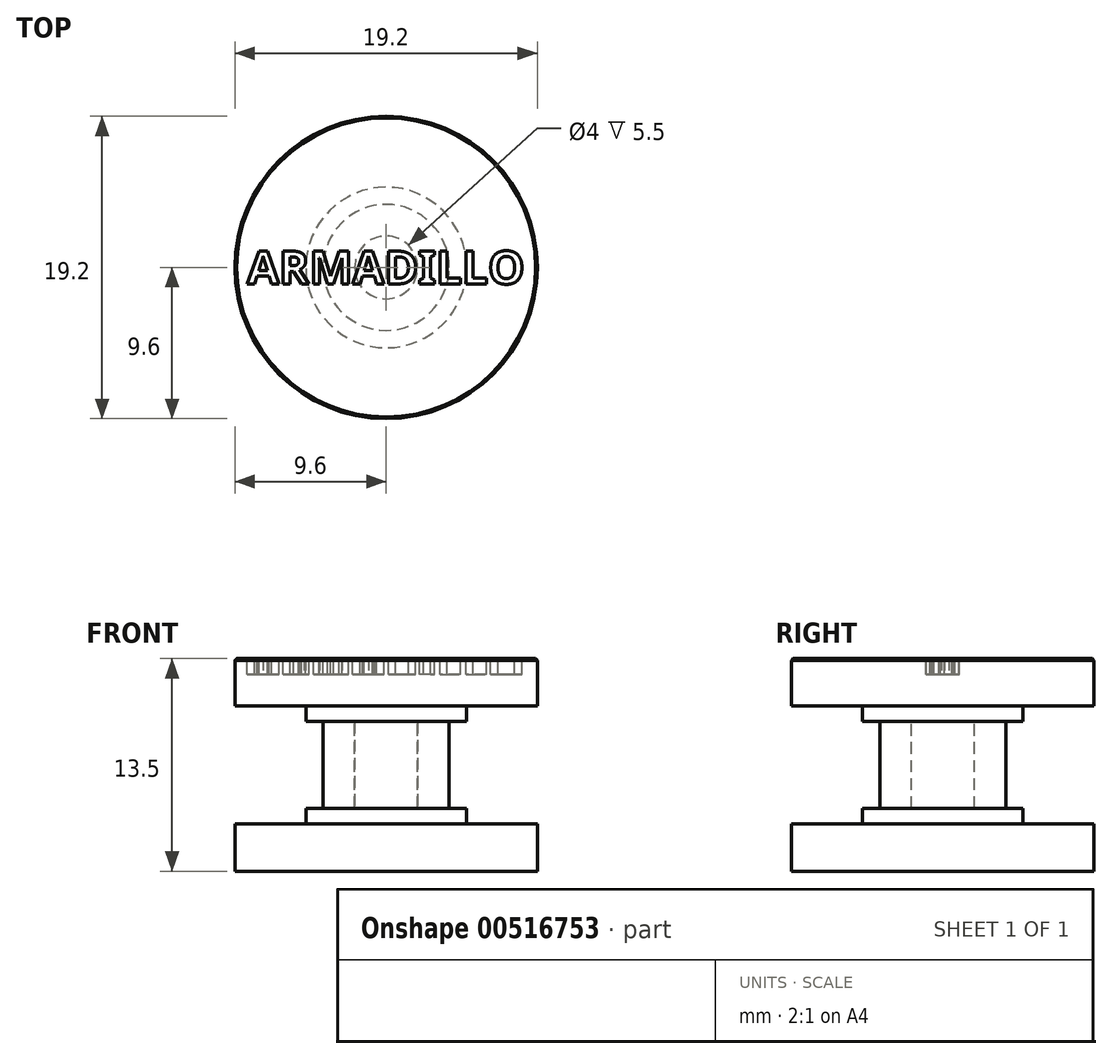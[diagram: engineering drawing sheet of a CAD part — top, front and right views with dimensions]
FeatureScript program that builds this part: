
annotation { "Feature Type Name" : "Feature", "Feature Type Description" : "" }
export const myFeature = defineFeature(function(context is Context, id is Id, definition is map)
    precondition{}
    {
        {
            var Q0;
            Q0=qCreatedBy(makeId("Front.planeOp"),FACE);
            var sketch = newSketch(context, id + "F0", { "sketchPlane" : qUnion([Q0])});
            skLineSegment(sketch, "E0", {"start": v(0, 5.5) * mm, "end": v(0, 9.5) * mm});
            skLineSegment(sketch, "E1", {"start": v(0, 9.5) * mm, "end": v(9.6, 9.5) * mm});
            skLineSegment(sketch, "E2", {"start": v(9.6, 9.5) * mm, "end": v(9.6, 6.5) * mm});
            skLineSegment(sketch, "E3", {"start": v(9.6, 6.5) * mm, "end": v(5.1, 6.5) * mm});
            skLineSegment(sketch, "E4", {"start": v(5.1, 6.5) * mm, "end": v(5.1, 5.5) * mm});
            skLineSegment(sketch, "E5", {"start": v(5.1, 5.5) * mm, "end": v(4, 5.5) * mm});
            skLineSegment(sketch, "E6", {"start": v(4, 5.5) * mm, "end": v(4, 0) * mm});
            skLineSegment(sketch, "E7", {"start": v(4, 0) * mm, "end": v(2, 0) * mm});
            skLineSegment(sketch, "E8.bottom", {"start": v(0, 5.5) * mm, "end": v(2, 5.5) * mm});
            skLineSegment(sketch, "E8.right", {"start": v(2, 5.5) * mm, "end": v(2, 0) * mm});
            skPoint(sketch, "E9.orphan", {"position": v(0, 0) * mm});
            skLineSegment(sketch, "E10.bottom", {"start": v(2, 0) * mm, "end": v(5.1, 0) * mm});
            skLineSegment(sketch, "E10.right", {"start": v(5.1, 0) * mm, "end": v(5.1, -1) * mm});
            skLineSegment(sketch, "E11.bottom", {"start": v(5.1, -1) * mm, "end": v(9.6, -1) * mm});
            skLineSegment(sketch, "E11.top", {"start": v(0, -4) * mm, "end": v(9.6, -4) * mm});
            skLineSegment(sketch, "E11.right", {"start": v(9.6, -1) * mm, "end": v(9.6, -4) * mm});
            skLineSegment(sketch, "E12", {"start": v(0, 5.5) * mm, "end": v(0, -4) * mm});
            skSolve(sketch);
        }
        {
            var Q0;
            Q0=makeQuery(id+"F0.imprint","IMPRINT",FACE,{"disambiguationData":[TD([[makeQuery(id+"F0.imprint","IMPRINT",EDGE,{"derivedFrom":sQuery(id+"F0.wireOp",EDGE,"E0")}),-1.0]])]});
            var Q1;
            Q1=sQuery(id+"F0.wireOp",EDGE,"E0");
            revolve(context, id + "F1", {"entities" : qUnion([Q0]), "axis" : qUnion([Q1]), "revolveType" : RevolveType.FULL});
        }
        {
            var Q0;
            Q0=makeQuery(id+"F1.opRevolve","SWEPT_EDGE",EDGE,{"disambiguationData":[OSD([sQuery(id+"F0.wireOp",EDGE,"E1"),sQuery(id+"F0.wireOp",EDGE,"E2")])]});
            chamfer(context, id + "F2", {"entities" : qUnion([Q0]), "width" : 0.1 * mm, "tangentPropagation" : true});
        }
        {
            var Q0;
            Q0=makeQuery(id+"F1.opRevolve","SWEPT_FACE",FACE,{"disambiguationData":[OSD([sQuery(id+"F0.wireOp",EDGE,"E1")])]});
            var sketch = newSketch(context, id + "F3", { "sketchPlane" : qUnion([Q0])});
            skText(sketch, "E13", { "text": "ARMADILLO", "fontName": "NotoSans-Bold.ttf"});
            skPoint(sketch, "E14", {"position": v(0, 0) * mm});
            const initialGuessF3  = {"E13": [-0.00882, -0.00105, 1, 0, 0.0021]};
            skSetInitialGuess(sketch, initialGuessF3);
            skSolve(sketch);
        }
        {
            var Q0;
            Q0=qSketchRegion(id+"F3",true);
            extrude(context, id + "F4", {"entities" : qUnion([Q0]), "operationType" : NewBodyOperationType.REMOVE, "oppositeDirection" : true, "depth" : 1 * mm, "offsetDistance" : 25 * mm});
        }
        {
            var Q0;
            Q0=makeQuery(id+"F0.imprint","IMPRINT",FACE,{"disambiguationData":[TD([[makeQuery(id+"F0.imprint","IMPRINT",EDGE,{"derivedFrom":sQuery(id+"F0.wireOp",EDGE,"E8.bottom")}),-1.0]])]});
            var Q1;
            Q1=sQuery(id+"F0.wireOp",EDGE,"E12");
            revolve(context, id + "F5", {"entities" : qUnion([Q0]), "axis" : qUnion([Q1]), "revolveType" : RevolveType.FULL});
        }
    });
